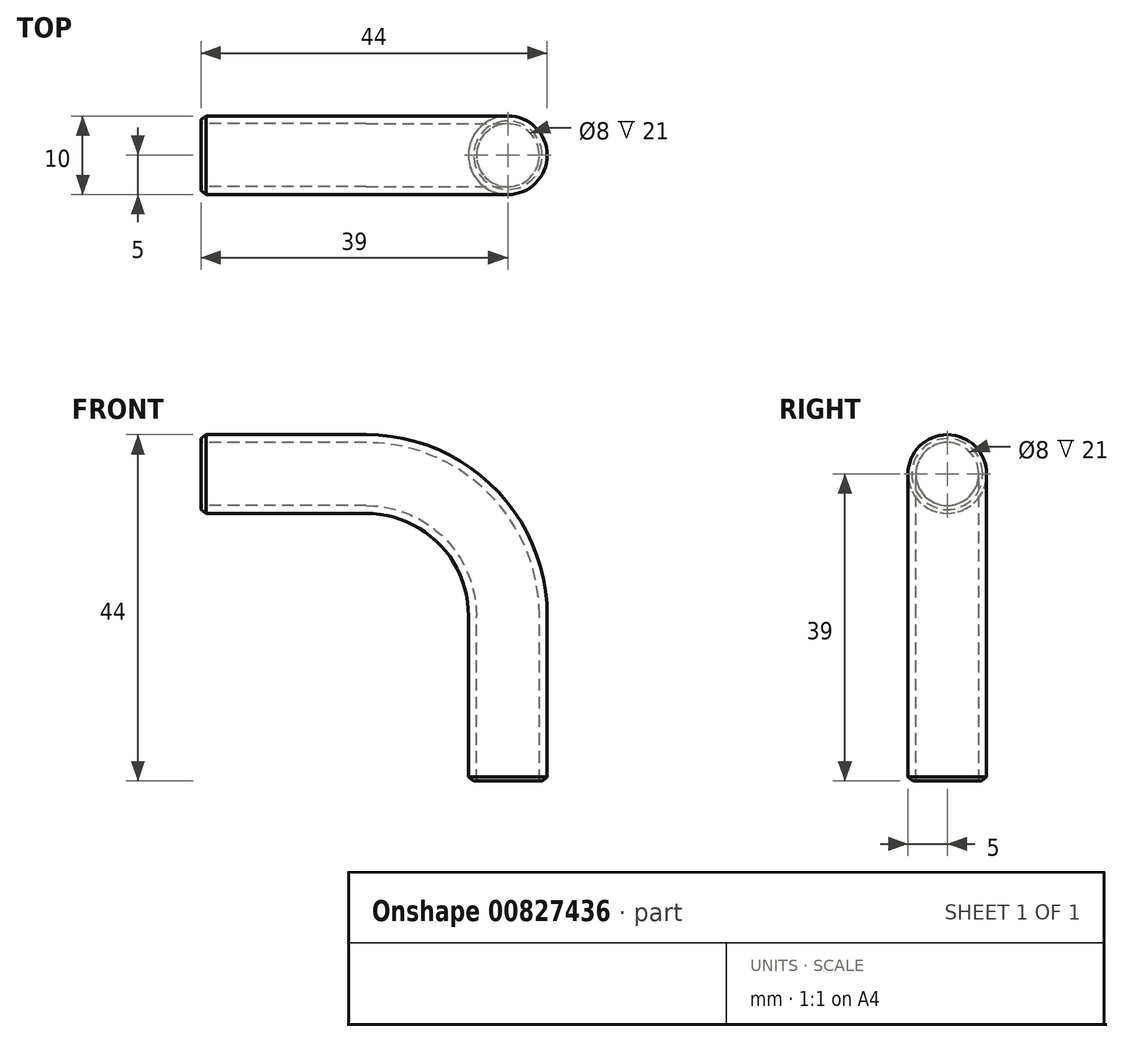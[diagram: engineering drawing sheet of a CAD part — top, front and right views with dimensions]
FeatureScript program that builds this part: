
annotation { "Feature Type Name" : "Feature", "Feature Type Description" : "" }
export const myFeature = defineFeature(function(context is Context, id is Id, definition is map)
    precondition{}
    {
        {
            var Q0;
            Q0=qCreatedBy(makeId("Top.planeOp"),FACE);
            var sketch = newSketch(context, id + "F0", { "sketchPlane" : qUnion([Q0])});
            skCircle(sketch, "E0", {"center": v(0, 0) * mm, "radius": 5 * mm});
            skCircle(sketch, "E1", {"center": v(0, 0) * mm, "radius": 4 * mm});
            skSolve(sketch);
        }
        {
            var Q0;
            Q0=qCreatedBy(makeId("Front.planeOp"),FACE);
            var sketch = newSketch(context, id + "F1", { "sketchPlane" : qUnion([Q0])});
            skArc(sketch, "E2", {"start": v(0, 21) * mm, "mid": v(-5.27, 33.73) * mm, "end": v(-18, 39) * mm});
            skLineSegment(sketch, "E3", {"start": v(-18, 39) * mm, "end": v(-39, 39) * mm});
            skLineSegment(sketch, "E4", {"start": v(0, 21) * mm, "end": v(0, 0) * mm});
            skSolve(sketch);
        }
        {
            var Q0;
            Q0=makeQuery(id+"F0.imprint","IMPRINT",FACE,{"disambiguationData":[TD([[makeQuery(id+"F0.imprint","IMPRINT",EDGE,{"derivedFrom":sQuery(id+"F0.wireOp",EDGE,"E0")}),1.0]])]});
            var Q1;
            Q1=sQuery(id+"F1.wireOp",EDGE,"E4");
            var Q2;
            Q2=sQuery(id+"F1.wireOp",EDGE,"E2");
            var Q3;
            Q3=sQuery(id+"F1.wireOp",EDGE,"E3");
            sweep(context, id + "F2", {"profiles" : qUnion([Q0]), "path" : qUnion([Q1, Q2, Q3])});
        }
        {
            var Q0;
            Q0=makeQuery(id+"F2.opSweep","CAP_EDGE",EDGE,{"disambiguationData":[OSD([sQuery(id+"F0.wireOp",EDGE,"E0"),sQuery(id+"F1.wireOp",VERTEX,"E3.end")])],"isStart":false});
            var Q1;
            Q1=makeQuery(id+"F2.opSweep","CAP_EDGE",EDGE,{"disambiguationData":[OSD([sQuery(id+"F0.wireOp",EDGE,"E0"),sQuery(id+"F1.wireOp",VERTEX,"E4.end")])],"isStart":true});
            chamfer(context, id + "F3", {"entities" : qUnion([Q0, Q1]), "chamferType" : ChamferType.OFFSET_ANGLE, "width" : .5 * mm, "oppositeDirection" : false, "angle" : 52.5 * degree, "tangentPropagation" : true});
        }
    });
